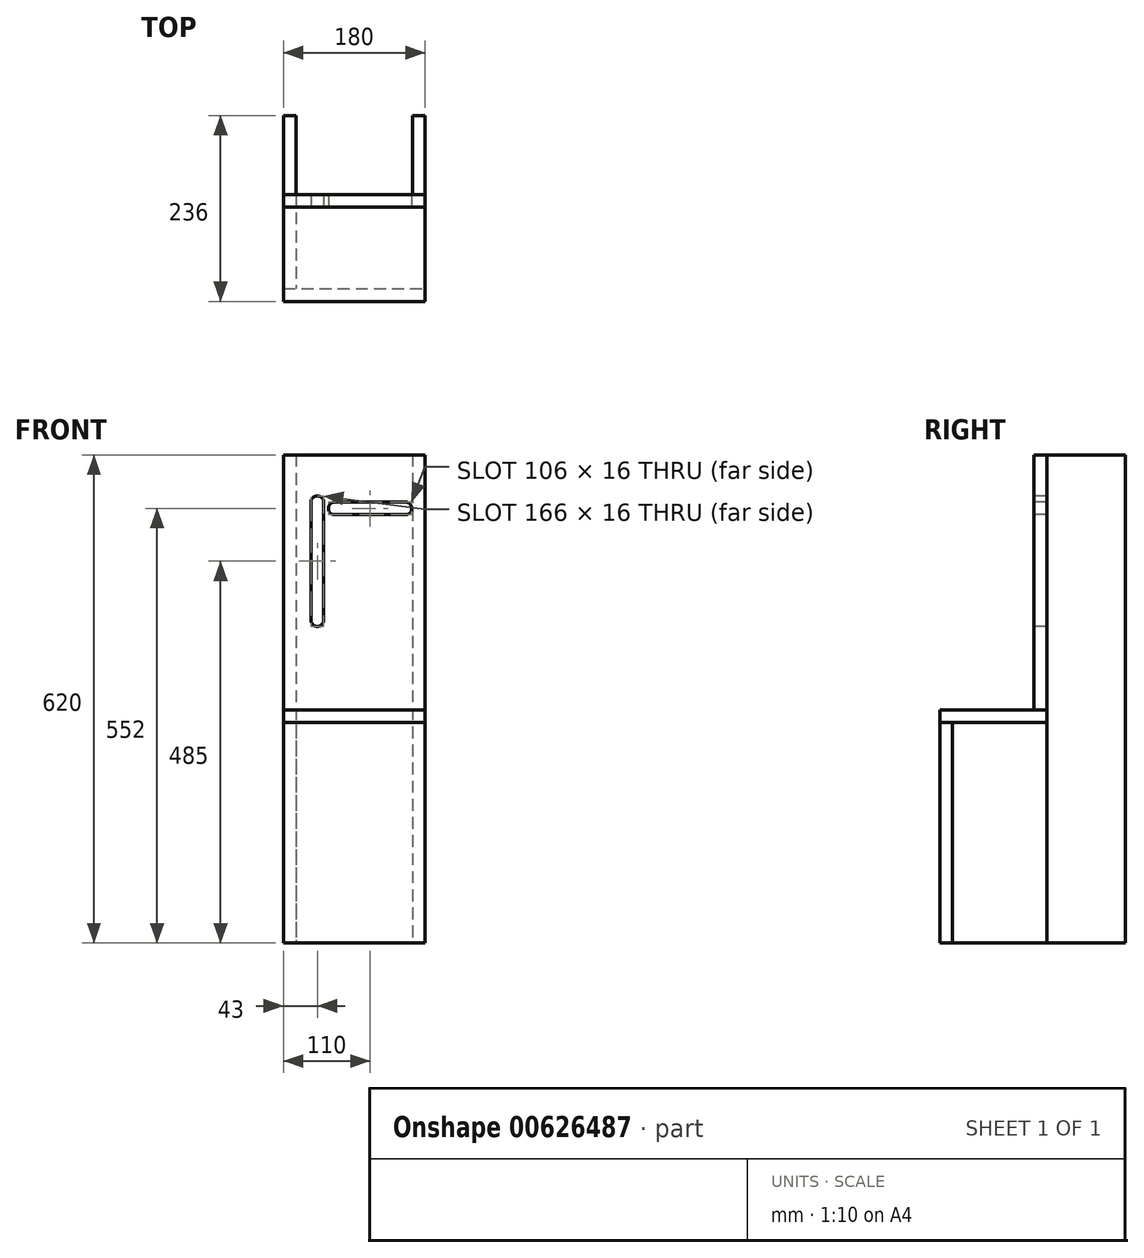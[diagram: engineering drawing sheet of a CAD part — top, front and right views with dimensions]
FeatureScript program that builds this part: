
annotation { "Feature Type Name" : "Feature", "Feature Type Description" : "" }
export const myFeature = defineFeature(function(context is Context, id is Id, definition is map)
    precondition{}
    {
        {
            var Q0;
            Q0=qCreatedBy(makeId("Top.planeOp"),FACE);
            var sketch = newSketch(context, id + "F0", { "sketchPlane" : qUnion([Q0])});
            skLineSegment(sketch, "E0.bottom", {"start": v(-90, 60) * mm, "end": v(-74, 60) * mm});
            skLineSegment(sketch, "E0.top", {"start": v(-90, -60) * mm, "end": v(-74, -60) * mm});
            skLineSegment(sketch, "E0.left", {"start": v(-90, 60) * mm, "end": v(-90, -60) * mm});
            skLineSegment(sketch, "E0.right", {"start": v(-74, 60) * mm, "end": v(-74, -60) * mm});
            skLineSegment(sketch, "E1.bottom", {"start": v(-90, -60) * mm, "end": v(90, -60) * mm});
            skLineSegment(sketch, "E1.top", {"start": v(-90, -76) * mm, "end": v(90, -76) * mm});
            skLineSegment(sketch, "E1.left", {"start": v(-90, -60) * mm, "end": v(-90, -76) * mm});
            skLineSegment(sketch, "E1.right", {"start": v(90, -60) * mm, "end": v(90, -76) * mm});
            skLineSegment(sketch, "E2.bottom", {"start": v(90, -60) * mm, "end": v(74, -60) * mm});
            skLineSegment(sketch, "E2.top", {"start": v(90, 60) * mm, "end": v(74, 60) * mm});
            skLineSegment(sketch, "E2.left", {"start": v(90, -60) * mm, "end": v(90, 60) * mm});
            skLineSegment(sketch, "E2.right", {"start": v(74, -60) * mm, "end": v(74, 60) * mm});
            skLineSegment(sketch, "E3.MirrorCS", {"start": v(74, 60) * mm, "end": v(74, -60) * mm});
            skLineSegment(sketch, "E4.top", {"start": v(-90, 160) * mm, "end": v(-74, 160) * mm});
            skLineSegment(sketch, "E4.left", {"start": v(-90, 60) * mm, "end": v(-90, 160) * mm});
            skLineSegment(sketch, "E4.right", {"start": v(-74, 60) * mm, "end": v(-74, 160) * mm});
            skLineSegment(sketch, "E5.top", {"start": v(90, 160) * mm, "end": v(74, 160) * mm});
            skLineSegment(sketch, "E5.left", {"start": v(90, 60) * mm, "end": v(90, 160) * mm});
            skLineSegment(sketch, "E5.right", {"start": v(74, 60) * mm, "end": v(74, 160) * mm});
            skSolve(sketch);
        }
        {
            var Q0;
            Q0=makeQuery(id+"F0.imprint","IMPRINT",FACE,{"disambiguationData":[TD([[makeQuery(id+"F0.imprint","IMPRINT",EDGE,{"derivedFrom":sQuery(id+"F0.wireOp",EDGE,"E0.bottom")}),-1.0]])]});
            var Q1;
            Q1=makeQuery(id+"F0.imprint","IMPRINT",FACE,{"disambiguationData":[TD([[makeQuery(id+"F0.imprint","IMPRINT",EDGE,{"derivedFrom":sQuery(id+"F0.wireOp",EDGE,"E2.bottom")}),-1.0]])]});
            var Q2;
            {var subQ0=sQuery(id+"F0.wireOp",EDGE,"E0.left");Q2=makeQuery(id+"F0.imprint","IMPRINT",FACE,{"disambiguationData":[TD([[makeQuery(id+"F0.imprint","IMPRINT",EDGE,{"derivedFrom":subQ0}),1.0]])]});}
            extrude(context, id + "F1", {"entities" : qUnion([Q0, Q1, Q2]), "depth" : 280 * mm, "offsetDistance" : 25 * mm});
        }
        {
            var Q0;
            Q0=makeQuery(id+"F0.imprint","IMPRINT",FACE,{"disambiguationData":[TD([[makeQuery(id+"F0.imprint","IMPRINT",EDGE,{"derivedFrom":sQuery(id+"F0.wireOp",EDGE,"E0.bottom")}),1.0]])]});
            var Q1;
            Q1=makeQuery(id+"F0.imprint","IMPRINT",FACE,{"disambiguationData":[TD([[makeQuery(id+"F0.imprint","IMPRINT",EDGE,{"derivedFrom":sQuery(id+"F0.wireOp",EDGE,"E2.top")}),-1.0]])]});
            extrude(context, id + "F2", {"entities" : qUnion([Q0, Q1]), "depth" : 620 * mm, "offsetDistance" : 25 * mm});
        }
        {
            var Q0;
            Q0=makeQuery(id+"F0.imprint","IMPRINT",FACE,{"disambiguationData":[TD([[makeQuery(id+"F0.imprint","IMPRINT",EDGE,{"derivedFrom":sQuery(id+"F0.wireOp",EDGE,"E1.top")}),1.0]])]});
            var Q1;
            Q1=makeQuery(id+"F1.opExtrude","CAP_FACE",FACE,{"disambiguationData":[OSD([sQuery(id+"F0.wireOp",EDGE,"E0.left"),sQuery(id+"F0.wireOp",EDGE,"E0.right"),sQuery(id+"F0.wireOp",EDGE,"E1.bottom"),sQuery(id+"F0.wireOp",EDGE,"E0.bottom")])],"isStart":false});
            extrude(context, id + "F3", {"entities" : qUnion([Q0]), "endBound" : BoundingType.UP_TO_SURFACE, "depth" : 25 * mm, "endBoundEntityFace" : qUnion([Q1]), "offsetDistance" : 25 * mm});
        }
        {
            var Q0;
            Q0=makeQuery(id+"F1.opExtrude","CAP_FACE",FACE,{"disambiguationData":[OSD([sQuery(id+"F0.wireOp",EDGE,"E0.left"),sQuery(id+"F0.wireOp",EDGE,"E0.right"),sQuery(id+"F0.wireOp",EDGE,"E1.bottom"),sQuery(id+"F0.wireOp",EDGE,"E1.top"),sQuery(id+"F0.wireOp",EDGE,"E1.left"),sQuery(id+"F0.wireOp",EDGE,"E1.right"),sQuery(id+"F0.wireOp",EDGE,"E2.left"),sQuery(id+"F0.wireOp",EDGE,"E3.MirrorCS"),sQuery(id+"F0.wireOp",EDGE,"E0.bottom"),sQuery(id+"F0.wireOp",EDGE,"E2.top")])],"isStart":false});
            var sketch = newSketch(context, id + "F4", { "sketchPlane" : qUnion([Q0])});
            skLineSegment(sketch, "E6.bottom", {"start": v(-90, -76) * mm, "end": v(90, -76) * mm});
            skLineSegment(sketch, "E6.top", {"start": v(-90, 60) * mm, "end": v(90, 60) * mm});
            skLineSegment(sketch, "E6.left", {"start": v(-90, -76) * mm, "end": v(-90, 60) * mm});
            skLineSegment(sketch, "E6.right", {"start": v(90, -76) * mm, "end": v(90, 60) * mm});
            skSolve(sketch);
        }
        {
            var Q0;
            Q0=makeQuery(id+"F4.imprint","IMPRINT",FACE,{"disambiguationData":[TD([[makeQuery(id+"F4.imprint","IMPRINT",EDGE,{"derivedFrom":sQuery(id+"F4.wireOp",EDGE,"E6.bottom")}),1.0]])]});
            var Q1;
            {var subQ1=makeQuery(id+"F1.opExtrude","CAP_EDGE",EDGE,{"disambiguationData":[OSD([sQuery(id+"F0.wireOp",EDGE,"E0.right")])],"isStart":false});Q1=makeQuery(id+"F4.imprint","IMPRINT",FACE,{"disambiguationData":[TD([[makeQuery(id+"F4.imprint","IMPRINT",EDGE,{"derivedFrom":subQ1}),1.0]])]});}
            var Q2;
            {var subQ3=makeQuery(id+"F1.opExtrude","CAP_EDGE",EDGE,{"disambiguationData":[OSD([sQuery(id+"F0.wireOp",EDGE,"E0.right")])],"isStart":false});Q2=makeQuery(id+"F4.imprint","IMPRINT",FACE,{"disambiguationData":[TD([[makeQuery(id+"F4.imprint","IMPRINT",EDGE,{"derivedFrom":subQ3}),-1.0]])]});}
            extrude(context, id + "F5", {"entities" : qUnion([Q0, Q1, Q2]), "depth" : 16 * mm, "offsetDistance" : 25 * mm});
        }
        {
            var Q0;
            Q0=makeQuery(id+"F5.opExtrude","CAP_FACE",FACE,{"disambiguationData":[OSD([sQuery(id+"F4.wireOp",EDGE,"E6.bottom"),sQuery(id+"F4.wireOp",EDGE,"E6.top"),sQuery(id+"F4.wireOp",EDGE,"E6.left"),sQuery(id+"F4.wireOp",EDGE,"E6.right")])],"isStart":false});
            var sketch = newSketch(context, id + "F6", { "sketchPlane" : qUnion([Q0])});
            skLineSegment(sketch, "E7.bottom", {"start": v(-90, 60) * mm, "end": v(90, 60) * mm});
            skLineSegment(sketch, "E7.top", {"start": v(-90, 44) * mm, "end": v(90, 44) * mm});
            skLineSegment(sketch, "E7.left", {"start": v(-90, 60) * mm, "end": v(-90, 44) * mm});
            skLineSegment(sketch, "E7.right", {"start": v(90, 60) * mm, "end": v(90, 44) * mm});
            skSolve(sketch);
        }
        {
            var Q0;
            Q0=makeQuery(id+"F6.imprint","IMPRINT",FACE,{"disambiguationData":[TD([[makeQuery(id+"F6.imprint","IMPRINT",EDGE,{"derivedFrom":sQuery(id+"F6.wireOp",EDGE,"E7.bottom")}),-1.0]])]});
            var Q1;
            Q1=makeQuery(id+"F2.opExtrude","CAP_FACE",FACE,{"disambiguationData":[OSD([sQuery(id+"F0.wireOp",EDGE,"E0.bottom"),sQuery(id+"F0.wireOp",EDGE,"E4.top"),sQuery(id+"F0.wireOp",EDGE,"E4.left"),sQuery(id+"F0.wireOp",EDGE,"E4.right")])],"isStart":false});
            extrude(context, id + "F7", {"entities" : qUnion([Q0]), "endBound" : BoundingType.UP_TO_SURFACE, "depth" : 25 * mm, "endBoundEntityFace" : qUnion([Q1]), "offsetDistance" : 25 * mm});
        }
        {
            var Q0;
            Q0=makeQuery(id+"F7.opExtrude","SWEPT_FACE",FACE,{"disambiguationData":[OSD([sQuery(id+"F6.wireOp",EDGE,"E7.top")])]});
            var sketch = newSketch(context, id + "F8", { "sketchPlane" : qUnion([Q0])});
            skLineSegment(sketch, "E8", {"start": v(-55, 560) * mm, "end": v(-55, 410) * mm});
            skArc(sketch, "E9", {"start": v(-39, 560) * mm, "mid": v(-47, 568) * mm, "end": v(-55, 560) * mm});
            skArc(sketch, "E10", {"start": v(-55, 410) * mm, "mid": v(-47, 402) * mm, "end": v(-39, 410) * mm});
            skLineSegment(sketch, "E11", {"start": v(-39, 410) * mm, "end": v(-39, 560) * mm});
            skLineSegment(sketch, "E12", {"start": v(-25, 560) * mm, "end": v(65, 560) * mm});
            skArc(sketch, "E13", {"start": v(65, 544) * mm, "mid": v(73, 552) * mm, "end": v(65, 560) * mm});
            skLineSegment(sketch, "E14", {"start": v(65, 544) * mm, "end": v(-25, 544) * mm});
            skArc(sketch, "E15", {"start": v(-25, 560) * mm, "mid": v(-33, 552) * mm, "end": v(-25, 544) * mm});
            skSolve(sketch);
        }
        {
            var Q0;
            Q0=makeQuery(id+"F8.imprint","IMPRINT",FACE,{"disambiguationData":[TD([[makeQuery(id+"F8.imprint","IMPRINT",EDGE,{"derivedFrom":sQuery(id+"F8.wireOp",EDGE,"E12")}),-1.0]])]});
            var Q1;
            Q1=makeQuery(id+"F8.imprint","IMPRINT",FACE,{"disambiguationData":[TD([[makeQuery(id+"F8.imprint","IMPRINT",EDGE,{"derivedFrom":sQuery(id+"F8.wireOp",EDGE,"E8")}),1.0]])]});
            var Q2;
            Q2=makeQuery(id+"F7.opExtrude","SWEPT_FACE",FACE,{"disambiguationData":[OSD([sQuery(id+"F6.wireOp",EDGE,"E7.bottom")])]});
            extrude(context, id + "F9", {"entities" : qUnion([Q0, Q1]), "operationType" : NewBodyOperationType.REMOVE, "endBound" : BoundingType.UP_TO_SURFACE, "oppositeDirection" : true, "depth" : 25 * mm, "endBoundEntityFace" : qUnion([Q2]), "offsetDistance" : 25 * mm});
        }
    });
